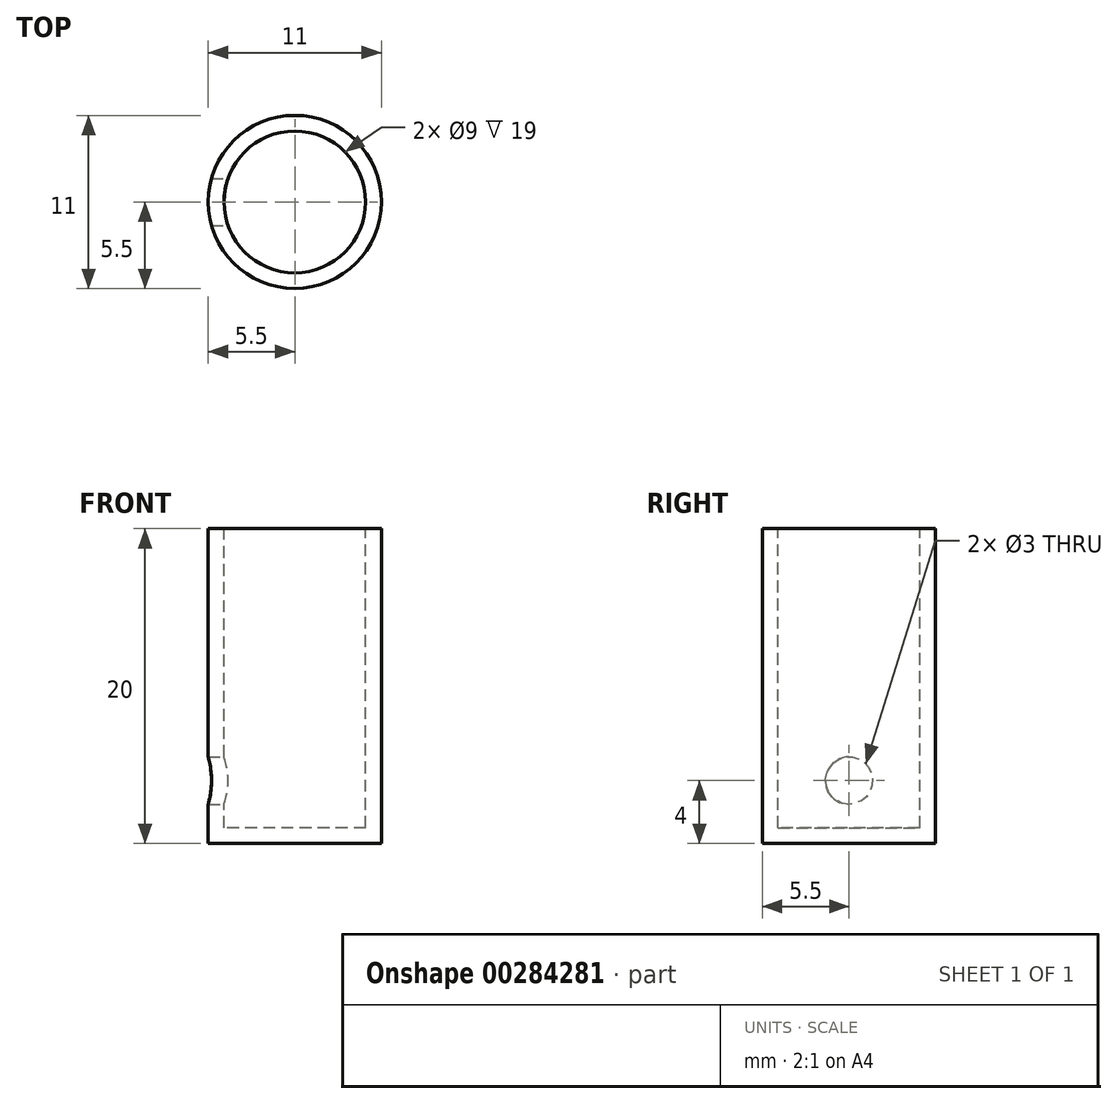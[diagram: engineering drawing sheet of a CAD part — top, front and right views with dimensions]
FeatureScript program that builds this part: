
annotation { "Feature Type Name" : "Feature", "Feature Type Description" : "" }
export const myFeature = defineFeature(function(context is Context, id is Id, definition is map)
    precondition{}
    {
        {
            var Q0;
            Q0=qCreatedBy(makeId("Top.planeOp"),FACE);
            var sketch = newSketch(context, id + "F0", { "sketchPlane" : qUnion([Q0])});
            skCircle(sketch, "E0", {"center": v(0, 0) * mm, "radius": 5.5 * mm});
            skSolve(sketch);
        }
        {
            var Q0;
            Q0=makeQuery(id+"F0.imprint","IMPRINT",FACE,{"disambiguationData":[TD([[makeQuery(id+"F0.imprint","IMPRINT",EDGE,{"derivedFrom":sQuery(id+"F0.wireOp",EDGE,"E0")}),1.0]])]});
            extrude(context, id + "F1", {"entities" : qUnion([Q0]), "depth" : 20 * mm});
        }
        {
            var Q0;
            Q0=makeQuery(id+"F1.opExtrude","CAP_FACE",FACE,{"disambiguationData":[OSD([sQuery(id+"F0.wireOp",EDGE,"E0")])],"isStart":false});
            var sketch = newSketch(context, id + "F2", { "sketchPlane" : qUnion([Q0])});
            skCircle(sketch, "E1", {"center": v(0, 0) * mm, "radius": 4.5 * mm});
            skSolve(sketch);
        }
        {
            var Q0;
            Q0=makeQuery(id+"F2.imprint","IMPRINT",FACE,{"disambiguationData":[TD([[makeQuery(id+"F2.imprint","IMPRINT",EDGE,{"derivedFrom":sQuery(id+"F2.wireOp",EDGE,"E1")}),1.0]])]});
            extrude(context, id + "F3", {"entities" : qUnion([Q0]), "operationType" : NewBodyOperationType.REMOVE, "oppositeDirection" : true, "depth" : 19 * mm});
        }
        {
            var Q0;
            Q0=qCreatedBy(makeId("Right.planeOp"),FACE);
            var sketch = newSketch(context, id + "F4", { "sketchPlane" : qUnion([Q0])});
            skCircle(sketch, "E2", {"center": v(0, 4) * mm, "radius": 1.5 * mm});
            skSolve(sketch);
        }
        {
            var Q0;
            Q0 = qSketchRegion(id + "F4", true);
            extrude(context, id + "F5", {"entities" : qUnion([Q0]), "operationType" : NewBodyOperationType.REMOVE, "oppositeDirection" : true, "depth" : 25 * mm});
        }
    });
